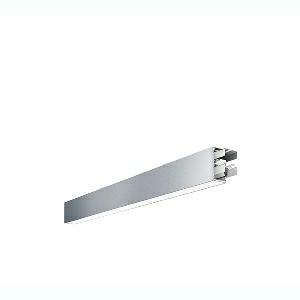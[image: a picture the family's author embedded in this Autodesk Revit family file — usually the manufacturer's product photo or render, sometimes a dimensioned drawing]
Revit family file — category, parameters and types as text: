
# Revit family: dotoo_line_-_dla_2000_830_d_sta_00807967_c479
name_source: partatom
category: Lighting Fixtures
units: mm (PartAtom-declared; Revit-internal decimal feet)

## family parameters
Cut with Voids When Loaded = No
Host = Face
Light Source = No
Part Type = Normal
Room Calculation Point = No
Round Connector Dimension = Use Diameter
Shared = No

## types (1)
- DOTOO.line - DLA 2000/830/D STA (1 x LED, 1650 lm, 3000K)
    Apparent Load = 16 VA
    Approval mark = CE
    CIE Flux Codes = 67 91 98 100 100
    Color Rendering = 80-89
    Color Temperature = 3000K
    Control Gear = Electronic ballast
    Default Elevation = 1800 mm
    Description = DLA 2000/830/D|Surface-mounted luminaire.|light source: LED|work equipment: Adjustable electronic ballast, digital DALI|connected load: 220-240 V, 50/60 Hz|Power consumption: approx. 16 W|luminous flux: 1650 lm|luminous efficacy: 103 lm/W|light distribution: Direct|colour temperature: Warm white, ca. 3000 K|class of protection: I|technology: Continuously dimmable|mains lead: Connector|glare control: Prism aperture|special features: DALI Load 1x, TouchDIM - dimming via standard switch, Through-wired, up to 18 m on one mains connection, Flicker-free, Suitable as emergency lighting, Start luminaire with mains connection, Mechanical and electrical connection of the individual modules without tools|
    Frequency = 50 Hz
    Height = 110 mm
    Lamp = 1 x LED
    Lamp Light Flux = 1650 lm
    Lamp count = 1
    Length = 1408 mm
    Luminous efficacy = 103 lm/W
    Manufacturer = Waldmann
    ModVariant = No
    Model = 00807967
    Mounting Place = Ceiling
    Mounting Type = Surface mounted
    Number of Poles = 1
    OnlyDefault = Yes
    Power Factor = 1
    Product Name = DOTOO.line - DLA 2000/830/D STA
    Product group = Ceiling mounted luminaire
    ProductGroupID = 3
    Protection Class = Protection class I
    Protection Degree = IP 40
    RLX_Detail_Level = 1
    RLX_Emergency_Light_Flux = 0 lm
    RLX_Emergency_Type = 0
    RLX_Emergency_Type_DB = No
    RlxData = <blob elided: 18365 chars, md5=edc71bf1>
    Socket = socket
    Standby Power = 0 W
    System Light Flux = 1650 lm
    System Power = 16 W
    Type Comments = Product without accessories
    Type Image = 114372000-00807949.jpg
    URL = http://relux.com
    VarID = ---
    Voltage = 230 V
    Voltage Range = 220-240 V
    Weight = 0.00 kg
    Width = 60 mm  [stored 0.19685 ft]

note: [stored X ft] marks values corroborated as IEEE doubles in the binary element streams (Revit-internal decimal feet)

## geometry (parser evidence)
native form markers: Blend x4, Sweep x11
no freeform markers — native parametric forms only
